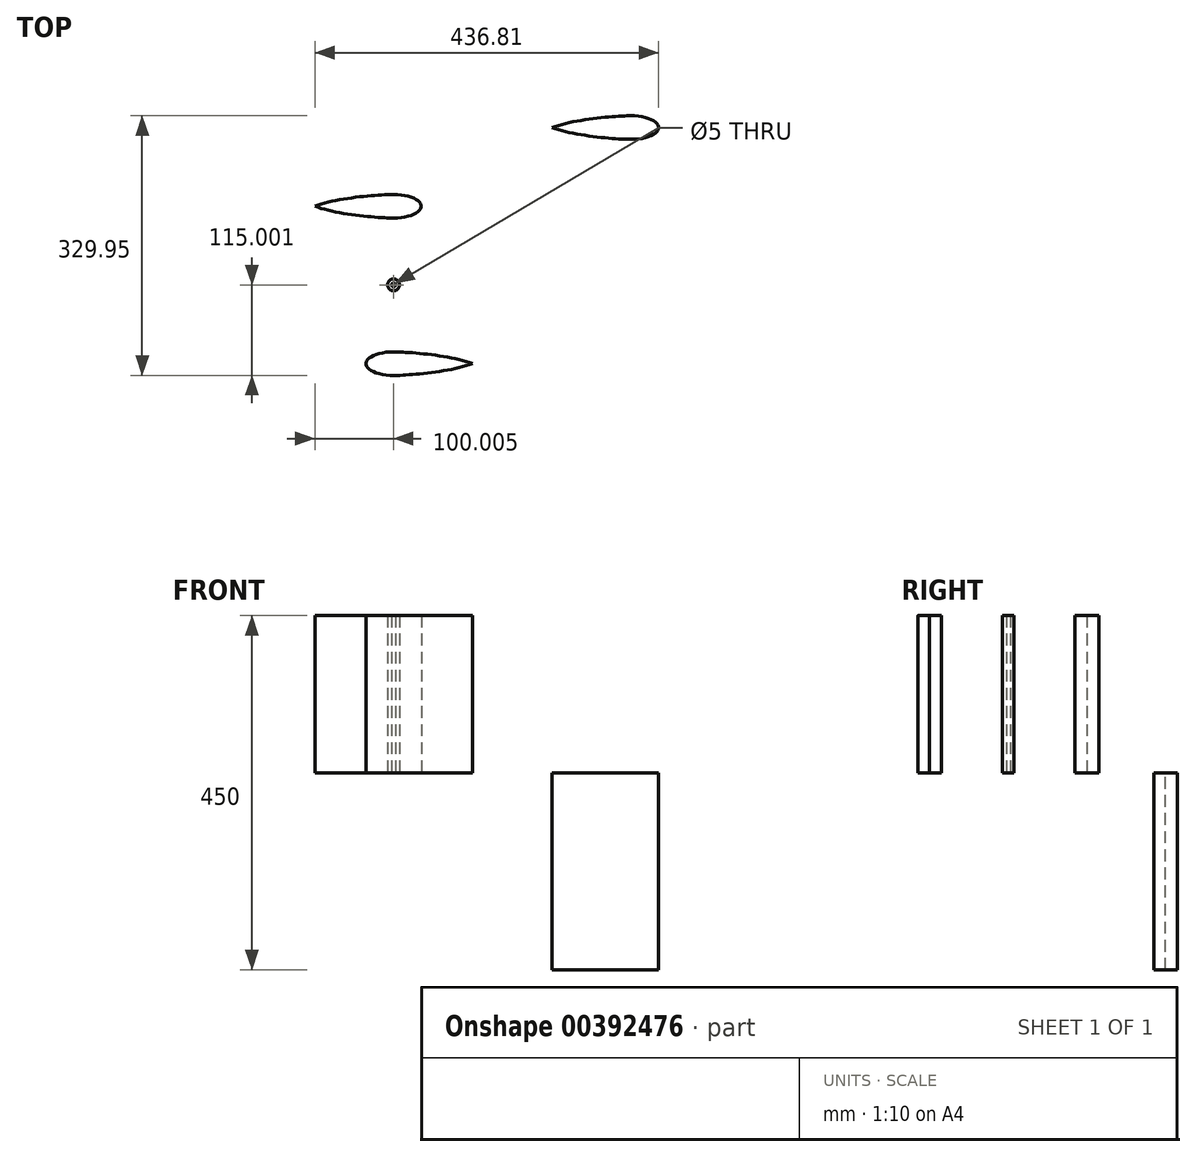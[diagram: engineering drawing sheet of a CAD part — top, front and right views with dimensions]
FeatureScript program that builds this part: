
annotation { "Feature Type Name" : "Feature", "Feature Type Description" : "" }
export const myFeature = defineFeature(function(context is Context, id is Id, definition is map)
    precondition{}
    {
        {
            var Q0;
            Q0=qCreatedBy(makeId("Top.planeOp"),FACE);
            var sketch = newSketch(context, id + "F0", { "sketchPlane" : qUnion([Q0])});
            skPoint(sketch, "E0", {"position": v(-100, 0) * mm});
            skPoint(sketch, "E1", {"position": v(0, 15) * mm});
            skPoint(sketch, "E2", {"position": v(0, -15) * mm});
            skFitSpline(sketch, "E3", {"points": [v(0, 15) * mm, v(-100, 0) * mm], "startDerivative": vector(-48.7, 0) * mm, "endDerivative": vector(-85.27, -32.97) * mm});
            skFitSpline(sketch, "E4.MirrorCS", {"points": [v(0, -15) * mm, v(-100, 0) * mm], "startDerivative": vector(-48.7, 0) * mm, "endDerivative": vector(-85.27, 32.97) * mm});
            skLineSegment(sketch, "E5", {"start": v(0, -15) * mm, "end": v(0, -15) * mm});
            skEllipticalArc(sketch, "E6", {});
            skLineSegment(sketch, "E7", {"start": v(-35.33, 0) * mm, "end": v(-35.33, 0) * mm});
            skLineSegment(sketch, "E8", {"start": v(0, 15) * mm, "end": v(0, 15) * mm});
            skPoint(sketch, "E9", {"position": v(35.33, 0) * mm});
            skPoint(sketch, "E10", {"position": v(-401.48, -99.95) * mm});
            skPoint(sketch, "E11", {"position": v(-301.48, -84.95) * mm});
            skPoint(sketch, "E12", {"position": v(-301.48, -114.95) * mm});
            skFitSpline(sketch, "E13", {"points": [v(-301.48, -84.95) * mm, v(-401.48, -99.95) * mm], "startDerivative": vector(-48.7, 0) * mm, "endDerivative": vector(-85.27, -32.97) * mm});
            skFitSpline(sketch, "E14.MirrorCS", {"points": [v(-301.48, -114.95) * mm, v(-401.48, -99.95) * mm], "startDerivative": vector(-48.7, 0) * mm, "endDerivative": vector(-85.27, 32.97) * mm});
            skLineSegment(sketch, "E15", {"start": v(-301.48, -114.95) * mm, "end": v(-301.48, -114.95) * mm});
            skEllipticalArc(sketch, "E16", {});
            skLineSegment(sketch, "E17", {"start": v(-336.8, -99.95) * mm, "end": v(-336.8, -99.95) * mm});
            skLineSegment(sketch, "E18", {"start": v(-301.48, -84.95) * mm, "end": v(-301.48, -84.95) * mm});
            skPoint(sketch, "E19", {"position": v(-266.14, -99.95) * mm});
            skLineSegment(sketch, "E20", {"start": v(-464.24, -199.95) * mm, "end": v(-112.76, -199.95) * mm, "construction": true});
            skPoint(sketch, "E21.MirrorP", {"position": v(-301.35, -284.95) * mm});
            skPoint(sketch, "E22.MirrorP", {"position": v(-301.35, -314.95) * mm});
            skPoint(sketch, "E23.MirrorP", {"position": v(-536.8, -299.95) * mm});
            skPoint(sketch, "E24.MirrorP", {"position": v(-201.35, -299.95) * mm});
            skEllipticalArc(sketch, "E25.MirrorCS", {});
            skFitSpline(sketch, "E26.MirrorCS", {"points": [v(-301.35, -284.95) * mm, v(-201.35, -299.95) * mm], "startDerivative": vector(48.7, 0) * mm, "endDerivative": vector(85.27, -32.97) * mm});
            skFitSpline(sketch, "E27.MirrorCS", {"points": [v(-301.35, -314.95) * mm, v(-201.35, -299.95) * mm], "startDerivative": vector(48.7, 0) * mm, "endDerivative": vector(85.27, 32.97) * mm});
            skFitSpline(sketch, "E28.MirrorCS", {"points": [v(-301.48, -114.95) * mm, v(-401.48, -99.95) * mm], "startDerivative": vector(-48.7, 0) * mm, "endDerivative": vector(-85.27, 32.97) * mm});
            skLineSegment(sketch, "E29", {"start": v(-301.48, -20.77) * mm, "end": v(-301.48, -408.4) * mm, "construction": true});
            skLineSegment(sketch, "E30", {"start": v(-183.8, -299.95) * mm, "end": v(-578.16, -299.95) * mm, "construction": true});
            skPoint(sketch, "E31", {"position": v(-301.48, -199.95) * mm});
            skCircle(sketch, "E32", {"center": v(-301.48, -199.95) * mm, "radius": 0.01 * mm});
            skCircle(sketch, "E33", {"center": v(-301.48, -199.95) * mm, "radius": 0.03 * mm});
            skCircle(sketch, "E34", {"center": v(-301.48, -199.95) * mm, "radius": 2.5 * mm});
            skCircle(sketch, "E35", {"center": v(-301.48, -199.95) * mm, "radius": 7.5 * mm});
            const initialGuessF0  = {"E6": [0, 0, 0, 1, 0.015, 0.03533193841576576, 3.141592653589793, 6.283185307179586], "E16": [-0.30147545073621745, -0.09994924572644104, 0, 1, 0.015, 0.03533193841576576, 3.141592653589793, 6.283185307179586], "E25.MirrorCS": [-0.301353581188726, -0.2999492457264411, 0, 1, 0.015, 0.03533193841576576, 6.283185307179586, 3.141592653589793], "E16": [-0.30147545073621745, -0.09994924572644104, 0, 1, 0.015, 0.03533193841576576, 3.141592653589793, 6.283185307179586]};
            skSetInitialGuess(sketch, initialGuessF0);
            skSolve(sketch);
        }
        {
            var Q0;
            Q0=makeQuery(id+"F0.imprint","IMPRINT",FACE,{"disambiguationData":[TD([[makeQuery(id+"F0.imprint","IMPRINT",EDGE,{"derivedFrom":sQuery(id+"F0.wireOp",EDGE,"E3")}),1.0]])]});
            extrude(context, id + "F1", {"entities" : qUnion([Q0]), "oppositeDirection" : true, "depth" : 250 * mm});
        }
        {
            var Q0;
            Q0=makeQuery(id+"F0.imprint","IMPRINT",FACE,{"disambiguationData":[TD([[makeQuery(id+"F0.imprint","IMPRINT",EDGE,{"derivedFrom":sQuery(id+"F0.wireOp",EDGE,"E16")}),1.0]])]});
            var Q1;
            Q1=makeQuery(id+"F0.imprint","IMPRINT",FACE,{"disambiguationData":[TD([[makeQuery(id+"F0.imprint","IMPRINT",EDGE,{"derivedFrom":sQuery(id+"F0.wireOp",EDGE,"E25.MirrorCS")}),1.0]])]});
            var Q2;
            Q2=makeQuery(id+"F0.imprint","IMPRINT",FACE,{"disambiguationData":[TD([[makeQuery(id+"F0.imprint","IMPRINT",EDGE,{"derivedFrom":sQuery(id+"F0.wireOp",EDGE,"E34")}),-1.0]])]});
            extrude(context, id + "F2", {"entities" : qUnion([Q0, Q1, Q2]), "depth" : 200 * mm});
        }
        {
            var Q0;
            Q0=qCreatedBy(makeId("Front.planeOp"),FACE);
            cPlane(context, id + "F3", {"entities" : qUnion([Q0]), "cplaneType" : CPlaneType.OFFSET, "offset" : 200 * mm, "width" : 150 * mm, "height" : 150 * mm});
        }
        {
            var Q0;
            Q0=qCreatedBy(id+"F3.planeOp",FACE);
            var sketch = newSketch(context, id + "F4", { "sketchPlane" : qUnion([Q0])});
            skLineSegment(sketch, "E36", {"start": v(-301.63, 0) * mm, "end": v(-301.63, 230.54) * mm, "construction": true});
            skCircle(sketch, "E37", {"center": v(-301.63, 185) * mm, "radius": 6 * mm});
            skCircle(sketch, "E38", {"center": v(-301.63, 15) * mm, "radius": 6 * mm});
            skLineSegment(sketch, "E39", {"start": v(-301.63, 191) * mm, "end": v(-319.29, 185) * mm});
            skLineSegment(sketch, "E40", {"start": v(-319.29, 185) * mm, "end": v(-301.63, 178.62) * mm});
            skLineSegment(sketch, "E41", {"start": v(-301.63, 178.62) * mm, "end": v(-283.97, 185) * mm});
            skLineSegment(sketch, "E42", {"start": v(-283.97, 185) * mm, "end": v(-301.63, 191) * mm});
            skSolve(sketch);
        }
        {
            var Q0;
            Q0=sQuery(id+"F4.wireOp",EDGE,"E37");
            var Q1;
            Q1=sQuery(id+"F4.wireOp",EDGE,"E38");
            extrude(context, id + "F5", {"bodyType" : ToolBodyType.SURFACE, "surfaceEntities" : qUnion([Q0, Q1]), "endBound" : BoundingType.SYMMETRIC, "depth" : 200 * mm});
        }
    });
